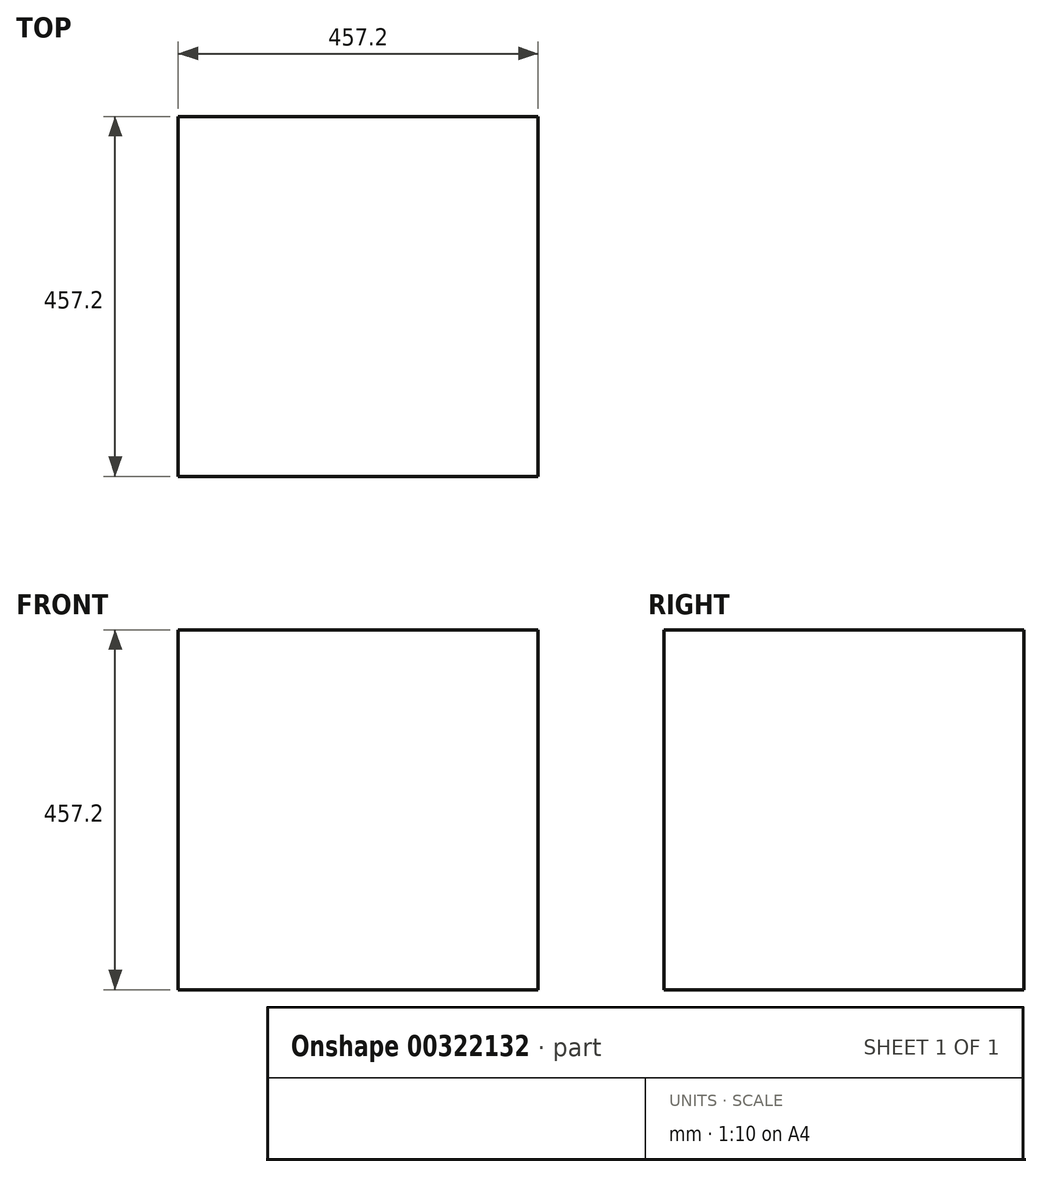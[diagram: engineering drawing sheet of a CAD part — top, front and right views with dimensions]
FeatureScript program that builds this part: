
annotation { "Feature Type Name" : "Feature", "Feature Type Description" : "" }
export const myFeature = defineFeature(function(context is Context, id is Id, definition is map)
    precondition{}
    {
        {
            var Q0;
            Q0=qCreatedBy(makeId("Top.planeOp"),FACE);
            var sketch = newSketch(context, id + "F0", { "sketchPlane" : qUnion([Q0])});
            skLineSegment(sketch, "E0.bottom", {"start": v(-228.6, 228.6) * mm, "end": v(228.6, 228.6) * mm});
            skLineSegment(sketch, "E0.top", {"start": v(-228.6, -228.6) * mm, "end": v(228.6, -228.6) * mm});
            skLineSegment(sketch, "E0.left", {"start": v(-228.6, 228.6) * mm, "end": v(-228.6, -228.6) * mm});
            skLineSegment(sketch, "E0.right", {"start": v(228.6, 228.6) * mm, "end": v(228.6, -228.6) * mm});
            skPoint(sketch, "E0.middle", {"position": v(0, 0) * mm});
            skSolve(sketch);
        }
        {
            var Q0;
            Q0=makeQuery(id+"F0.imprint","IMPRINT",FACE,{"disambiguationData":[TD([[makeQuery(id+"F0.imprint","IMPRINT",EDGE,{"derivedFrom":sQuery(id+"F0.wireOp",EDGE,"E0.bottom")}),-1.0]])]});
            extrude(context, id + "F1", {"entities" : qUnion([Q0]), "depth" : 457.2 * mm});
        }
    });
